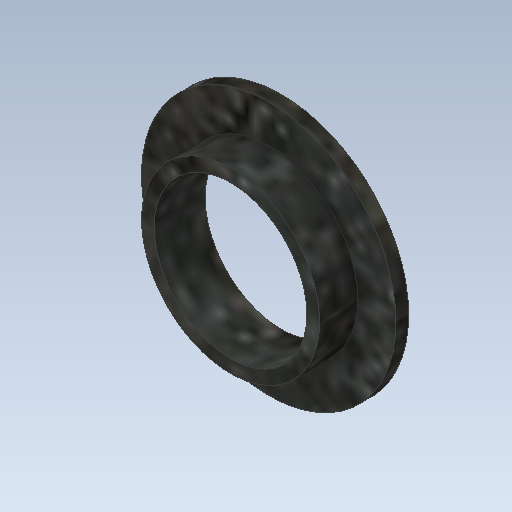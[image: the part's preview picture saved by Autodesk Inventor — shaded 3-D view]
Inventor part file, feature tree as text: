
AUTODESK INVENTOR PART (.ipt)
format: ipt  version: 2020.2 (Build 242310000, 310)  size: 172,032 bytes
history: native  units: mm
features: extrude x2, other x1, sketch x1
ambient origin geometry x8: Origin, YZ Plane, XZ Plane, XY Plane, X Axis, Y Axis, Z Axis, Center Point
bodies: Body1 (feature_tree)
feature tree (4):
  other  "ソリッド1"
  sketch  "スケッチ1"
  extrude  "押し出し1"  Depth=12.0mm
  extrude  "押し出し2"  Depth=14.0mm
